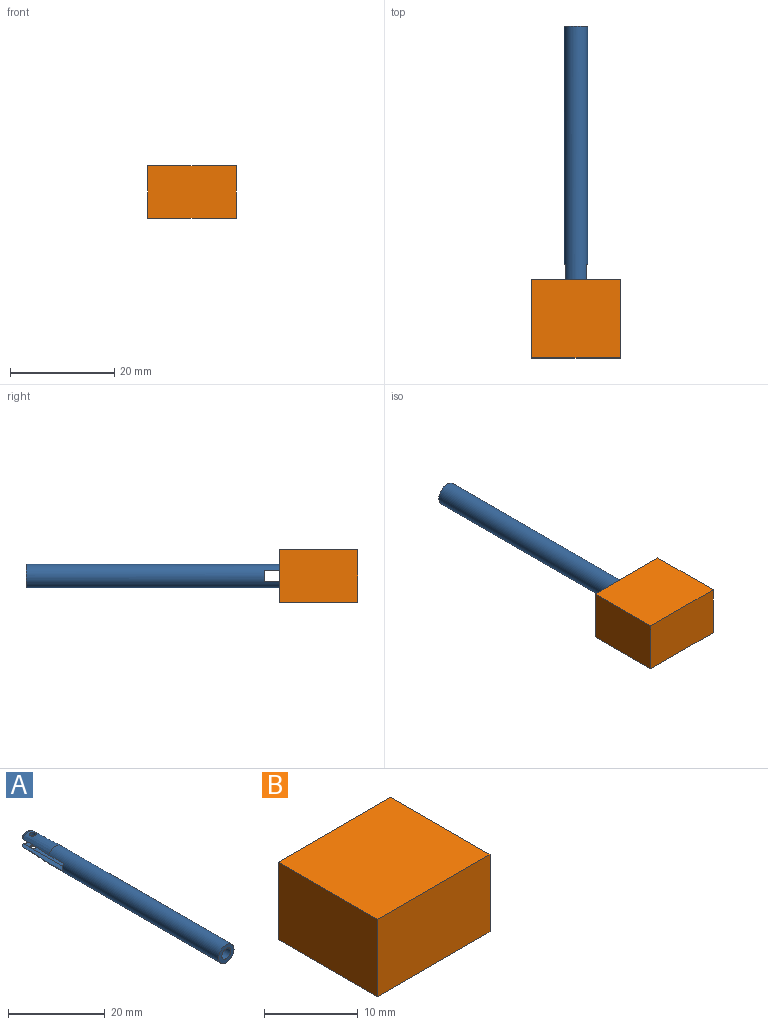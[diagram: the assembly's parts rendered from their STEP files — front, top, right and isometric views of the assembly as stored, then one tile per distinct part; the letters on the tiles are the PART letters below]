
ASSEMBLY  parts=2 mates=1
PART A: 17 faces, bbox 4.5x58.6x4.5 mm
  f0: cylinder r=1mm len=2mm, axis (0,0,1), area 2.1mm2, adj f8,f13
  f1: plane 12.91x1.2mm, normal (0,0,1), area 13.7mm2, adj f6,f8,f9,f11,f16
  f2: plane 12.91x1.2mm, normal (0,0,1), area 13.7mm2, adj f3,f6,f8,f11,f16
  f3: plane 2x1.42mm, normal (0,1,0), area 2mm2, adj f2,f6,f10,f11
  f4: plane 12.91x1.2mm, normal (0,0,-1), area 13.7mm2, adj f5,f6,f9,f11,f15
  f5: cone r=2.25mm half-angle=1.9deg, axis (0,-1,0), area 34.4mm2, adj f4,f6,f10,f14,f15
  f6: cylinder r=2.25mm len=50mm, axis (0,1,0), area 689.1mm2, adj f1,f2,f3,f4,f5,f7,f8,f9
  f7: plane 4.5x4.5mm, normal (0,-1,0), area 10.6mm2, adj f6,f11
  f8: cone r=2.25mm half-angle=1.9deg, axis (0,-1,0), area 32.7mm2, adj f0,f1,f2,f6,f16
  f9: plane 2x1.42mm, normal (0,1,0), area 2mm2, adj f1,f4,f6,f11
  f10: plane 12.91x1.2mm, normal (0,0,-1), area 13.7mm2, adj f3,f5,f6,f11,f15
  f11: cylinder r=1.3mm len=58.61mm, axis (0,1,0), area 416.7mm2, adj f1,f2,f3,f4,f7,f9,f10,f12
  f12: cylinder r=0.7mm len=1.4mm, axis (0,0,1), area 1.6mm2, adj f11,f13
  f13: plane 2x2mm, normal (0,0,-1), area 1.6mm2, adj f0,f12
  f14: cylinder r=0.7mm len=1.4mm, axis (0,0,-1), area 3.4mm2, adj f5,f11
  f15: torus R=1.23mm, axis (0,1,0), area 3.6mm2, adj f4,f5,f10,f11
  f16: torus R=1.23mm, axis (0,1,0), area 3.6mm2, adj f1,f2,f8,f11
PART B: 16 faces, bbox 17x15x10.1 mm
  f0: cylinder r=0.75mm len=1.5mm, axis (-1,0,0), area 3.1mm2, adj f1,f2,f9
  f1: extruded ~5x4.5mm, area 44.6mm2, adj f0,f2,f5,f6
  f2: bspline ~5x5mm, area 64.5mm2, adj f0,f1,f4,f6
  f3: plane 17.02x10.12mm, normal (0,1,0), area 111.6mm2, adj f5,f11,f12,f13,f14
  f4: plane 4.5x3mm, normal (0,1,0), area 10.6mm2, adj f2
  f5: bspline ~9x8.5mm, area 60mm2, adj f1,f3
  f6: cylinder r=0.75mm len=1.5mm, axis (-1,0,0), area 3.2mm2, adj f1,f2,f10
  f7: plane 0.5x0.5mm, normal (-1,0,0), area 0.2mm2, adj f10
  f8: plane 0.5x0.5mm, normal (1,0,0), area 0.2mm2, adj f9
  f9: cone r=0.25mm half-angle=45deg, axis (-1,0,0), area 2.2mm2, adj f0,f8
  f10: cone r=0.75mm half-angle=45deg, axis (1,0,0), area 2.2mm2, adj f6,f7
  f11: plane 15x10.1mm, normal (1,0,0), area 151.5mm2, adj f3,f12,f14,f15
  f12: plane 17x15mm, normal (0,0,1), area 255mm2, adj f3,f11,f13,f15
  f13: plane 15x10.1mm, normal (-1,0,0), area 151.5mm2, adj f3,f12,f14,f15
  f14: plane 17x15mm, normal (0,0,-1), area 255mm2, adj f3,f11,f13,f15
  f15: plane 17x10.1mm, normal (0,-1,0), area 171.7mm2, adj f11,f12,f13,f14
PLACE A rot(axis=(1,0,0),180deg) t=(6.67,10.19,-3.99)mm
PLACE B t=(6.67,6.46,-3.99)mm fixed
MATE slider A.f6 <-> B.f4  axis (0,-1,0) through (6.67,10.19,-3.99)mm
